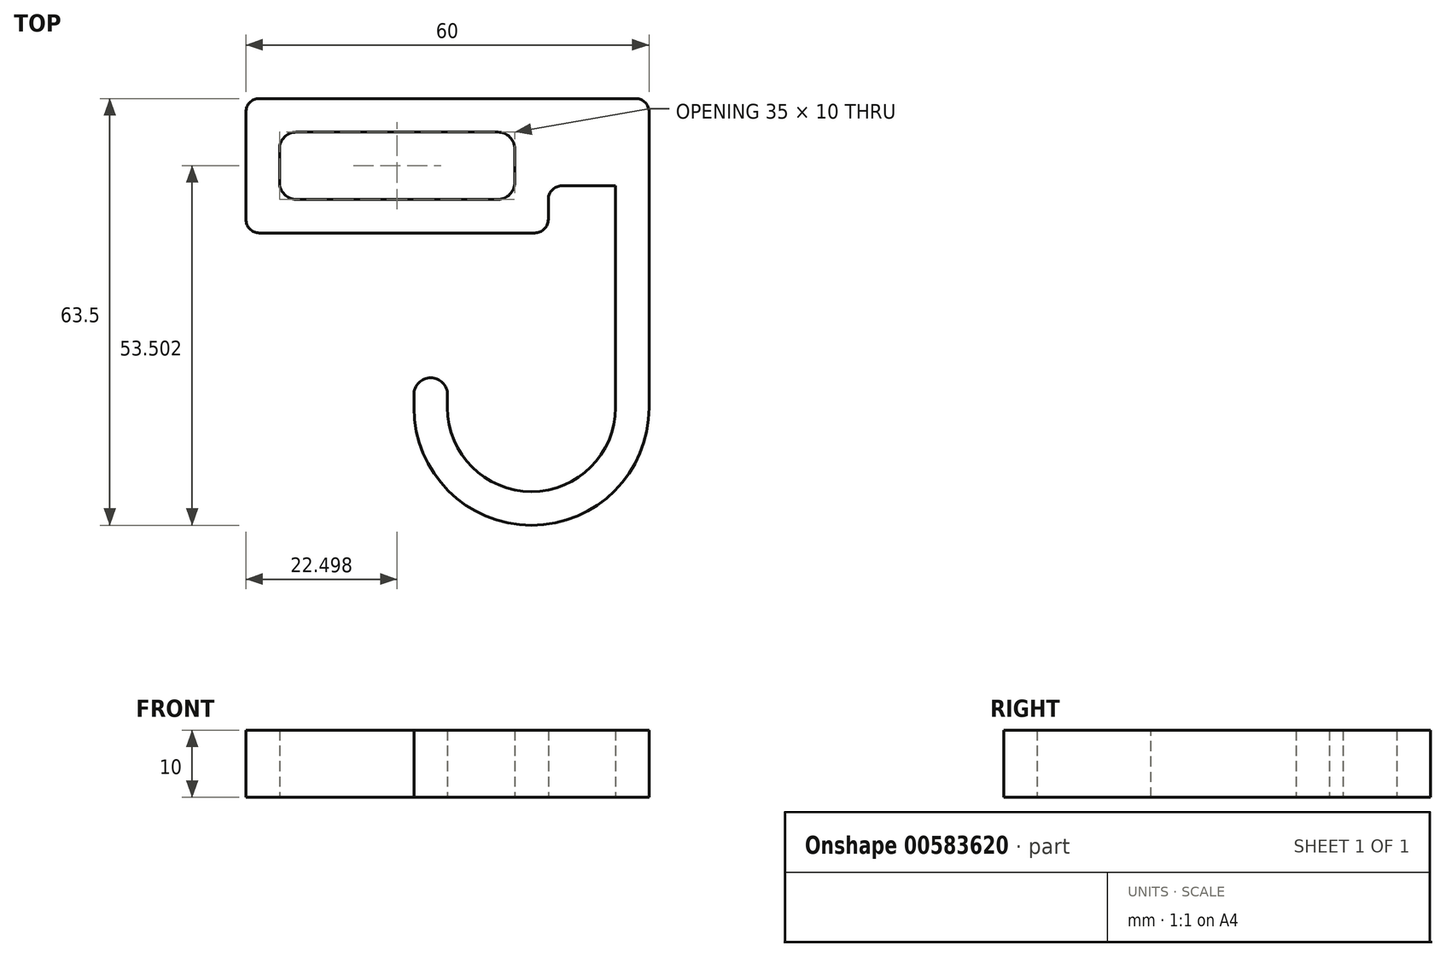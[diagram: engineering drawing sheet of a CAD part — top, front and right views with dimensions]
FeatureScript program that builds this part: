
annotation { "Feature Type Name" : "Feature", "Feature Type Description" : "" }
export const myFeature = defineFeature(function(context is Context, id is Id, definition is map)
    precondition{}
    {
        {
            var Q0;
            Q0=qCreatedBy(makeId("Top.planeOp"),FACE);
            var sketch = newSketch(context, id + "F0", { "sketchPlane" : qUnion([Q0])});
            skLineSegment(sketch, "E0.bottom", {"start": v(-23.4, -10.28) * mm, "end": v(21.6, -10.28) * mm});
            skLineSegment(sketch, "E0.top", {"start": v(-23.4, -25.28) * mm, "end": v(21.6, -25.28) * mm});
            skLineSegment(sketch, "E0.left", {"start": v(-23.4, -10.28) * mm, "end": v(-23.4, -25.28) * mm});
            skLineSegment(sketch, "E0.right", {"start": v(21.6, -10.28) * mm, "end": v(21.6, -25.28) * mm});
            skLineSegment(sketch, "E1.bottom", {"start": v(21.6, -10.28) * mm, "end": v(31.6, -10.28) * mm});
            skLineSegment(sketch, "E1.top", {"start": v(21.6, -18.28) * mm, "end": v(31.6, -18.28) * mm});
            skLineSegment(sketch, "E1.left", {"start": v(21.6, -10.28) * mm, "end": v(21.6, -18.28) * mm});
            skLineSegment(sketch, "E1.right", {"start": v(31.6, -10.28) * mm, "end": v(31.6, -18.28) * mm});
            skLineSegment(sketch, "E2.bottom", {"start": v(21.6, -18.28) * mm, "end": v(23.6, -18.28) * mm});
            skLineSegment(sketch, "E2.top", {"start": v(21.6, -10.28) * mm, "end": v(23.6, -10.28) * mm});
            skLineSegment(sketch, "E2.left", {"start": v(21.6, -18.28) * mm, "end": v(21.6, -10.28) * mm});
            skLineSegment(sketch, "E2.right", {"start": v(23.6, -18.28) * mm, "end": v(23.6, -10.28) * mm});
            skLineSegment(sketch, "E3.bottom", {"start": v(-23.4, -10.28) * mm, "end": v(36.6, -10.28) * mm});
            skLineSegment(sketch, "E3.top", {"start": v(-23.4, -5.28) * mm, "end": v(36.6, -5.28) * mm});
            skLineSegment(sketch, "E3.left", {"start": v(-23.4, -10.28) * mm, "end": v(-23.4, -5.28) * mm});
            skLineSegment(sketch, "E3.right", {"start": v(36.6, -10.28) * mm, "end": v(36.6, -5.28) * mm});
            skLineSegment(sketch, "E4.bottom", {"start": v(36.6, -10.28) * mm, "end": v(31.6, -10.28) * mm});
            skLineSegment(sketch, "E4.top", {"start": v(36.6, -36.28) * mm, "end": v(31.6, -36.28) * mm});
            skLineSegment(sketch, "E4.left", {"start": v(36.6, -10.28) * mm, "end": v(36.6, -36.28) * mm});
            skLineSegment(sketch, "E4.right", {"start": v(31.6, -10.28) * mm, "end": v(31.6, -36.28) * mm});
            skLineSegment(sketch, "E5.bottom", {"start": v(36.6, -36.28) * mm, "end": v(1.6, -36.28) * mm});
            skLineSegment(sketch, "E5.top", {"start": v(36.6, -68.78) * mm, "end": v(1.6, -68.78) * mm});
            skLineSegment(sketch, "E5.left", {"start": v(36.6, -36.28) * mm, "end": v(36.6, -68.78) * mm});
            skLineSegment(sketch, "E5.right", {"start": v(1.6, -36.28) * mm, "end": v(1.6, -68.78) * mm});
            skCircle(sketch, "E6", {"center": v(19.1, -51.28) * mm, "radius": 12.5 * mm});
            skLineSegment(sketch, "E7", {"start": v(31.6, -36.28) * mm, "end": v(31.6, -51.28) * mm});
            skLineSegment(sketch, "E8", {"start": v(6.6, -51.28) * mm, "end": v(6.6, -36.28) * mm});
            skLineSegment(sketch, "E9", {"start": v(1.6, -46.84) * mm, "end": v(31.6, -46.84) * mm});
            skLineSegment(sketch, "E10.bottom", {"start": v(-18.4, -10.28) * mm, "end": v(16.6, -10.28) * mm});
            skLineSegment(sketch, "E10.top", {"start": v(-18.4, -20.28) * mm, "end": v(16.6, -20.28) * mm});
            skLineSegment(sketch, "E10.left", {"start": v(-18.4, -10.28) * mm, "end": v(-18.4, -20.28) * mm});
            skLineSegment(sketch, "E10.right", {"start": v(16.6, -10.28) * mm, "end": v(16.6, -20.28) * mm});
            skSolve(sketch);
        }
        {
            var Q0;
            Q0=makeQuery(id+"F0.imprint","IMPRINT",FACE,{"disambiguationData":[TD([[makeQuery(id+"F0.imprint","IMPRINT",EDGE,{"derivedFrom":sQuery(id+"F0.wireOp",EDGE,"E0.top")}),1.0]])]});
            var Q1;
            Q1=makeQuery(id+"F0.imprint","IMPRINT",FACE,{"disambiguationData":[TD([[makeQuery(id+"F0.imprint","IMPRINT",EDGE,{"derivedFrom":sQuery(id+"F0.wireOp",EDGE,"E3.top")}),-1.0]])]});
            var Q2;
            {var subQ0=sQuery(id+"F0.wireOp",EDGE,"E1.top");Q2=makeQuery(id+"F0.imprint","IMPRINT",FACE,{"disambiguationData":[TD([[makeQuery(id+"F0.imprint","IMPRINT",EDGE,{"derivedFrom":subQ0}),1.0]])]});}
            var Q3;
            {var subQ2=sQuery(id+"F0.wireOp",EDGE,"E4.bottom");Q3=makeQuery(id+"F0.imprint","IMPRINT",FACE,{"disambiguationData":[TD([[makeQuery(id+"F0.imprint","IMPRINT",EDGE,{"derivedFrom":subQ2}),1.0]])]});}
            var Q4;
            {var subQ0=sQuery(id+"F0.wireOp",EDGE,"E4.top");Q4=makeQuery(id+"F0.imprint","IMPRINT",FACE,{"disambiguationData":[TD([[makeQuery(id+"F0.imprint","IMPRINT",EDGE,{"derivedFrom":subQ0}),-1.0]])]});}
            var Q5;
            {var subQ3=sQuery(id+"F0.wireOp",EDGE,"E4.top");Q5=makeQuery(id+"F0.imprint","IMPRINT",FACE,{"disambiguationData":[TD([[makeQuery(id+"F0.imprint","IMPRINT",EDGE,{"derivedFrom":subQ3}),1.0]])]});}
            var Q6;
            Q6=makeQuery(id+"F0.imprint","IMPRINT",FACE,{"disambiguationData":[TD([[makeQuery(id+"F0.imprint","IMPRINT",EDGE,{"derivedFrom":sQuery(id+"F0.wireOp",EDGE,"E5.top")}),-1.0]])]});
            extrude(context, id + "F1", {"entities" : qUnion([Q0, Q1, Q2, Q3, Q4, Q5, Q6]), "depth" : 10 * mm, "offsetDistance" : 25 * mm});
        }
        {
            var Q0;
            Q0=makeQuery(id+"F1.opExtrude","SWEPT_EDGE",EDGE,{"disambiguationData":[OSD([sQuery(id+"F0.wireOp",EDGE,"E0.top"),sQuery(id+"F0.wireOp",EDGE,"E0.left")])]});
            var Q1;
            Q1=makeQuery(id+"F1.opExtrude","SWEPT_EDGE",EDGE,{"disambiguationData":[OSD([sQuery(id+"F0.wireOp",EDGE,"E0.top"),sQuery(id+"F0.wireOp",EDGE,"E0.right")])]});
            var Q2;
            Q2=makeQuery(id+"F1.opExtrude","SWEPT_EDGE",EDGE,{"disambiguationData":[OSD([sQuery(id+"F0.wireOp",EDGE,"E1.top"),sQuery(id+"F0.wireOp",EDGE,"E2.bottom"),sQuery(id+"F0.wireOp",EDGE,"E2.right")])]});
            var Q3;
            Q3=makeQuery(id+"F1.opExtrude","SWEPT_EDGE",EDGE,{"disambiguationData":[OSD([sQuery(id+"F0.wireOp",EDGE,"E3.top"),sQuery(id+"F0.wireOp",EDGE,"E3.right")])]});
            var Q4;
            Q4=makeQuery(id+"F1.opExtrude","SWEPT_EDGE",EDGE,{"disambiguationData":[OSD([sQuery(id+"F0.wireOp",EDGE,"E3.top"),sQuery(id+"F0.wireOp",EDGE,"E3.left")])]});
            var Q5;
            Q5=makeQuery(id+"F1.opExtrude","SWEPT_EDGE",EDGE,{"disambiguationData":[OSD([sQuery(id+"F0.wireOp",EDGE,"NsWKEruK-m4Bu-zRWF-yN3X-Moidd9UuGFcL.right"),sQuery(id+"F0.wireOp",EDGE,"YJGLIIoB-hIYv-FKAd-DVHR-HEmebVhx8M1I")])]});
            var Q6;
            Q6=makeQuery(id+"F1.opExtrude","SWEPT_EDGE",EDGE,{"disambiguationData":[OSD([sQuery(id+"F0.wireOp",EDGE,"xUiY3VDc-dG26-37Mv-wh04-3zPwHl6UfaXe"),sQuery(id+"F0.wireOp",EDGE,"YJGLIIoB-hIYv-FKAd-DVHR-HEmebVhx8M1I")])]});
            fillet(context, id + "F2", {"entities" : qUnion([Q0, Q1, Q2, Q3, Q4, Q5, Q6]), "radius" : 2 * mm, "tangentPropagation" : true, "allowEdgeOverflow" : false});
        }
        {
            var Q0;
            Q0=makeQuery(id+"F1.opExtrude","SWEPT_EDGE",EDGE,{"disambiguationData":[OSD([sQuery(id+"F0.wireOp",EDGE,"E5.top"),sQuery(id+"F0.wireOp",EDGE,"E5.right")])]});
            var Q1;
            Q1=makeQuery(id+"F1.opExtrude","SWEPT_EDGE",EDGE,{"disambiguationData":[OSD([sQuery(id+"F0.wireOp",EDGE,"E5.top"),sQuery(id+"F0.wireOp",EDGE,"E5.left")])]});
            fillet(context, id + "F3", {"entities" : qUnion([Q0, Q1]), "radius" : 17.5 * mm, "tangentPropagation" : true, "allowEdgeOverflow" : false});
        }
        {
            var Q0;
            Q0=makeQuery(id+"F1.opExtrude","SWEPT_EDGE",EDGE,{"disambiguationData":[OSD([sQuery(id+"F0.wireOp",EDGE,"E5.right"),sQuery(id+"F0.wireOp",EDGE,"E9")])]});
            var Q1;
            Q1=makeQuery(id+"F1.opExtrude","SWEPT_EDGE",EDGE,{"disambiguationData":[OSD([sQuery(id+"F0.wireOp",EDGE,"E8"),sQuery(id+"F0.wireOp",EDGE,"E9")])]});
            var Q2;
            Q2=makeQuery(id+"F1.opExtrude","SWEPT_EDGE",EDGE,{"disambiguationData":[OSD([sQuery(id+"F0.wireOp",EDGE,"E10.top"),sQuery(id+"F0.wireOp",EDGE,"E10.left")])]});
            var Q3;
            Q3=makeQuery(id+"F1.opExtrude","SWEPT_EDGE",EDGE,{"disambiguationData":[OSD([sQuery(id+"F0.wireOp",EDGE,"E3.bottom"),sQuery(id+"F0.wireOp",EDGE,"E10.bottom"),sQuery(id+"F0.wireOp",EDGE,"E10.left")])]});
            var Q4;
            Q4=makeQuery(id+"F1.opExtrude","SWEPT_EDGE",EDGE,{"disambiguationData":[OSD([sQuery(id+"F0.wireOp",EDGE,"E3.bottom"),sQuery(id+"F0.wireOp",EDGE,"E10.bottom"),sQuery(id+"F0.wireOp",EDGE,"E10.right")])]});
            var Q5;
            Q5=makeQuery(id+"F1.opExtrude","SWEPT_EDGE",EDGE,{"disambiguationData":[OSD([sQuery(id+"F0.wireOp",EDGE,"E10.top"),sQuery(id+"F0.wireOp",EDGE,"E10.right")])]});
            fillet(context, id + "F4", {"entities" : qUnion([Q0, Q1, Q2, Q3, Q4, Q5]), "radius" : 2.5 * mm, "tangentPropagation" : true, "allowEdgeOverflow" : false});
        }
    });
